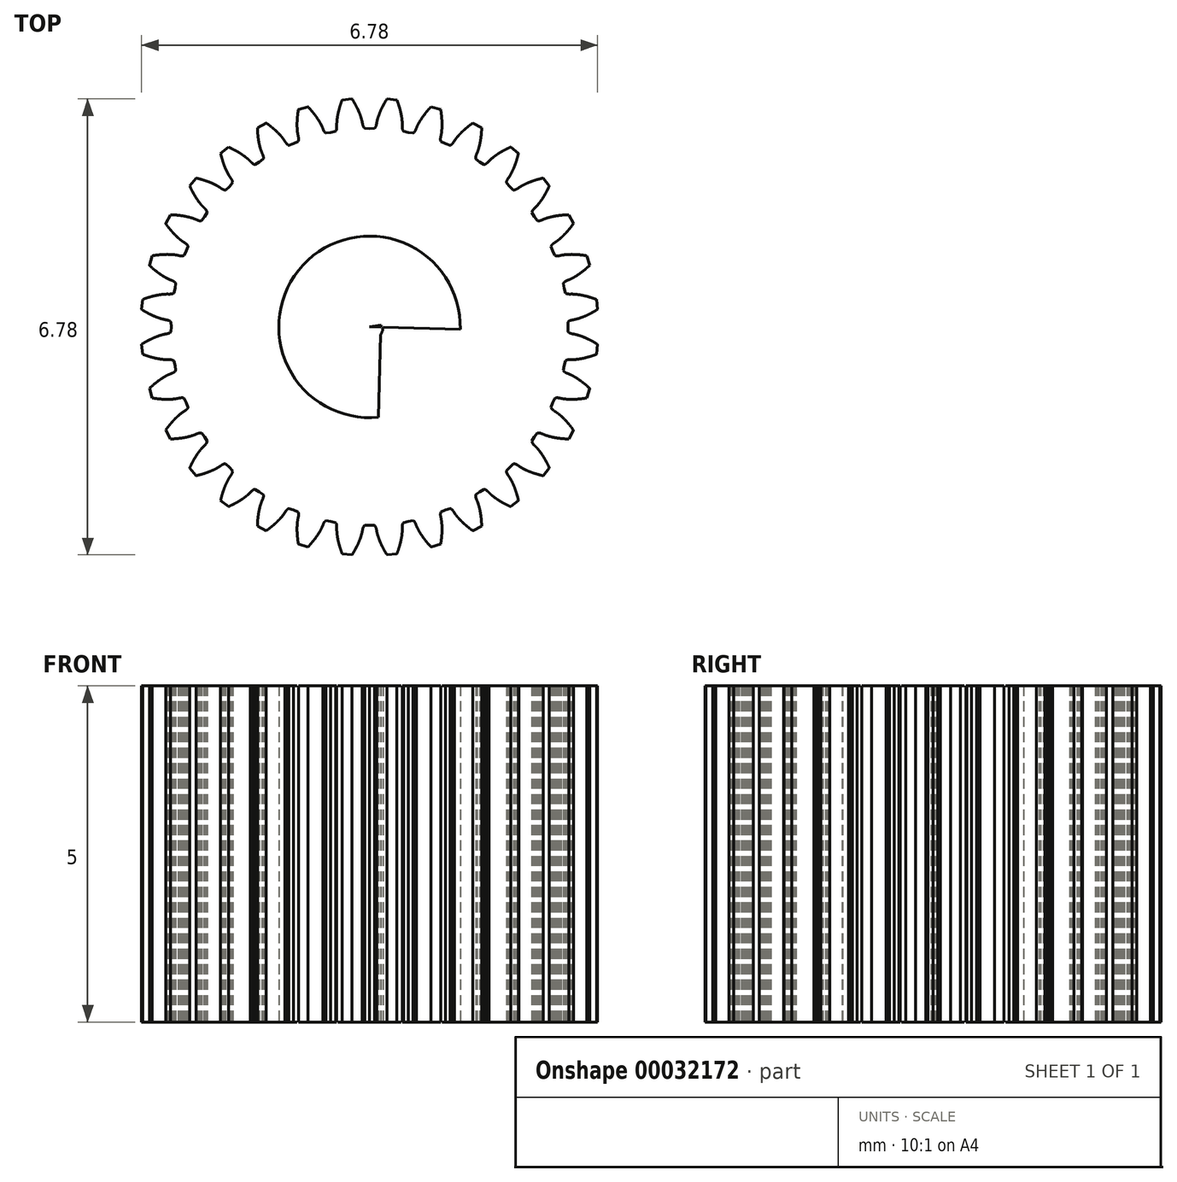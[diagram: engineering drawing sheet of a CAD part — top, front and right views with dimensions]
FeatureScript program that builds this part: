
annotation { "Feature Type Name" : "Feature", "Feature Type Description" : "" }
export const myFeature = defineFeature(function(context is Context, id is Id, definition is map)
    precondition{}
    {
        {
            var Q0;
            Q0=qCreatedBy(makeId("Top.planeOp"),FACE);
            var sketch = newSketch(context, id + "F0", { "sketchPlane" : qUnion([Q0])});
            skCircle(sketch, "E0", {"center": v(0, 0) * mm, "radius": 32.06 * mm});
            skCircle(sketch, "E1", {"center": v(0, 0) * mm, "radius": 0.2 * mm});
            skCircle(sketch, "E2", {"center": v(0, 0) * mm, "radius": 10.35 * mm});
            skCircle(sketch, "E3", {"center": v(0, 6.3) * mm, "radius": 0.2 * mm});
            skCircle(sketch, "E4", {"center": v(5.46, -3.15) * mm, "radius": 0.2 * mm});
            skCircle(sketch, "E5", {"center": v(-5.46, -3.15) * mm, "radius": 0.2 * mm});
            skLineSegment(sketch, "E6", {"start": v(0.26, 9.75) * mm, "end": v(0.26, 9.74) * mm});
            skLineSegment(sketch, "E7", {"start": v(0.26, 9.74) * mm, "end": v(0.26, 9.74) * mm});
            skLineSegment(sketch, "E8", {"start": v(0.26, 9.74) * mm, "end": v(0.26, 9.73) * mm});
            skLineSegment(sketch, "E9", {"start": v(0.26, 9.73) * mm, "end": v(0.25, 9.73) * mm});
            skLineSegment(sketch, "E10", {"start": v(0.25, 9.73) * mm, "end": v(0.25, 9.72) * mm});
            skLineSegment(sketch, "E11", {"start": v(0.25, 9.72) * mm, "end": v(0.25, 9.72) * mm});
            skLineSegment(sketch, "E12", {"start": v(0.25, 9.72) * mm, "end": v(0.25, 9.71) * mm});
            skLineSegment(sketch, "E13", {"start": v(0.25, 9.71) * mm, "end": v(0.24, 9.7) * mm});
            skLineSegment(sketch, "E14", {"start": v(0.24, 9.7) * mm, "end": v(0.24, 9.7) * mm});
            skLineSegment(sketch, "E15", {"start": v(0.24, 9.7) * mm, "end": v(0.24, 9.69) * mm});
            skLineSegment(sketch, "E16", {"start": v(0.24, 9.69) * mm, "end": v(0.23, 9.68) * mm});
            skLineSegment(sketch, "E17", {"start": v(0.23, 9.68) * mm, "end": v(0.23, 9.68) * mm});
            skLineSegment(sketch, "E18", {"start": v(0.23, 9.68) * mm, "end": v(0.23, 9.67) * mm});
            skLineSegment(sketch, "E19", {"start": v(0.23, 9.67) * mm, "end": v(0.23, 9.67) * mm});
            skLineSegment(sketch, "E20", {"start": v(0.23, 9.67) * mm, "end": v(0.22, 9.66) * mm});
            skLineSegment(sketch, "E21", {"start": v(0.22, 9.66) * mm, "end": v(0.22, 9.66) * mm});
            skLineSegment(sketch, "E22", {"start": v(0.22, 9.66) * mm, "end": v(0.22, 9.65) * mm});
            skLineSegment(sketch, "E23", {"start": v(0.22, 9.65) * mm, "end": v(0.22, 9.65) * mm});
            skLineSegment(sketch, "E24", {"start": v(0.22, 9.65) * mm, "end": v(0.22, 9.64) * mm});
            skLineSegment(sketch, "E25", {"start": v(0.22, 9.64) * mm, "end": v(0.21, 9.64) * mm});
            skLineSegment(sketch, "E26", {"start": v(0.21, 9.64) * mm, "end": v(0.21, 9.64) * mm});
            skLineSegment(sketch, "E27", {"start": v(0.21, 9.64) * mm, "end": v(0.21, 9.63) * mm});
            skLineSegment(sketch, "E28", {"start": v(0.21, 9.63) * mm, "end": v(0.2, 9.63) * mm});
            skLineSegment(sketch, "E29", {"start": v(0.2, 9.63) * mm, "end": v(0.2, 9.62) * mm});
            skLineSegment(sketch, "E30", {"start": v(0.2, 9.62) * mm, "end": v(0.2, 9.62) * mm});
            skLineSegment(sketch, "E31", {"start": v(0.2, 9.62) * mm, "end": v(0.2, 9.61) * mm});
            skLineSegment(sketch, "E32", {"start": v(0.2, 9.61) * mm, "end": v(0.2, 9.6) * mm});
            skLineSegment(sketch, "E33", {"start": v(0.2, 9.6) * mm, "end": v(0.2, 9.6) * mm});
            skLineSegment(sketch, "E34", {"start": v(0.2, 9.6) * mm, "end": v(0.2, 9.59) * mm});
            skLineSegment(sketch, "E35", {"start": v(0.2, 9.59) * mm, "end": v(0.2, 9.58) * mm});
            skLineSegment(sketch, "E36", {"start": v(0.2, 9.58) * mm, "end": v(0.19, 9.58) * mm});
            skLineSegment(sketch, "E37", {"start": v(0.19, 9.58) * mm, "end": v(0.19, 9.57) * mm});
            skLineSegment(sketch, "E38", {"start": v(0.19, 9.57) * mm, "end": v(0.18, 9.57) * mm});
            skLineSegment(sketch, "E39", {"start": v(0.18, 9.57) * mm, "end": v(0.18, 9.56) * mm});
            skLineSegment(sketch, "E40", {"start": v(0.18, 9.56) * mm, "end": v(0.18, 9.56) * mm});
            skLineSegment(sketch, "E41", {"start": v(0.18, 9.56) * mm, "end": v(0.18, 9.55) * mm});
            skLineSegment(sketch, "E42", {"start": v(0.18, 9.55) * mm, "end": v(0.18, 9.55) * mm});
            skLineSegment(sketch, "E43", {"start": v(0.18, 9.55) * mm, "end": v(0.17, 9.54) * mm});
            skLineSegment(sketch, "E44", {"start": v(0.17, 9.54) * mm, "end": v(0.17, 9.54) * mm});
            skLineSegment(sketch, "E45", {"start": v(0.17, 9.54) * mm, "end": v(0.17, 9.53) * mm});
            skLineSegment(sketch, "E46", {"start": v(0.17, 9.53) * mm, "end": v(0.17, 9.53) * mm});
            skLineSegment(sketch, "E47", {"start": v(0.17, 9.53) * mm, "end": v(0.17, 9.52) * mm});
            skLineSegment(sketch, "E48", {"start": v(0.17, 9.52) * mm, "end": v(0.16, 9.52) * mm});
            skLineSegment(sketch, "E49", {"start": v(0.16, 9.52) * mm, "end": v(0.16, 9.51) * mm});
            skLineSegment(sketch, "E50", {"start": v(0.16, 9.51) * mm, "end": v(0.16, 9.51) * mm});
            skLineSegment(sketch, "E51", {"start": v(0.16, 9.51) * mm, "end": v(0.16, 9.5) * mm});
            skLineSegment(sketch, "E52", {"start": v(0.16, 9.5) * mm, "end": v(0.16, 9.5) * mm});
            skLineSegment(sketch, "E53", {"start": v(0.16, 9.5) * mm, "end": v(0.15, 9.5) * mm});
            skLineSegment(sketch, "E54", {"start": v(0.15, 9.5) * mm, "end": v(0.15, 9.49) * mm});
            skLineSegment(sketch, "E55", {"start": v(0.15, 9.49) * mm, "end": v(0.15, 9.48) * mm});
            skLineSegment(sketch, "E56", {"start": v(0.15, 9.48) * mm, "end": v(0.15, 9.48) * mm});
            skLineSegment(sketch, "E57", {"start": v(0.15, 9.48) * mm, "end": v(0.15, 9.47) * mm});
            skLineSegment(sketch, "E58", {"start": v(0.15, 9.47) * mm, "end": v(0.15, 9.47) * mm});
            skLineSegment(sketch, "E59", {"start": v(0.15, 9.47) * mm, "end": v(0.14, 9.47) * mm});
            skLineSegment(sketch, "E60", {"start": v(0.14, 9.47) * mm, "end": v(0.14, 9.46) * mm});
            skLineSegment(sketch, "E61", {"start": v(0.14, 9.46) * mm, "end": v(0.14, 9.46) * mm});
            skLineSegment(sketch, "E62", {"start": v(0.14, 9.46) * mm, "end": v(0.14, 9.45) * mm});
            skLineSegment(sketch, "E63", {"start": v(0.14, 9.45) * mm, "end": v(0.14, 9.45) * mm});
            skLineSegment(sketch, "E64", {"start": v(0.14, 9.45) * mm, "end": v(0.14, 9.44) * mm});
            skLineSegment(sketch, "E65", {"start": v(0.14, 9.44) * mm, "end": v(0.13, 9.44) * mm});
            skLineSegment(sketch, "E66", {"start": v(0.13, 9.44) * mm, "end": v(0.13, 9.43) * mm});
            skLineSegment(sketch, "E67", {"start": v(0.13, 9.43) * mm, "end": v(0.13, 9.43) * mm});
            skLineSegment(sketch, "E68", {"start": v(0.13, 9.43) * mm, "end": v(0.13, 9.42) * mm});
            skLineSegment(sketch, "E69", {"start": v(0.13, 9.42) * mm, "end": v(0.13, 9.42) * mm});
            skLineSegment(sketch, "E70", {"start": v(0.13, 9.42) * mm, "end": v(0.12, 9.41) * mm});
            skLineSegment(sketch, "E71", {"start": v(0.12, 9.41) * mm, "end": v(0.12, 9.4) * mm});
            skLineSegment(sketch, "E72", {"start": v(0.12, 9.4) * mm, "end": v(0.12, 9.4) * mm});
            skLineSegment(sketch, "E73", {"start": v(0.12, 9.4) * mm, "end": v(0.12, 9.39) * mm});
            skLineSegment(sketch, "E74", {"start": v(0.12, 9.39) * mm, "end": v(0.12, 9.38) * mm});
            skLineSegment(sketch, "E75", {"start": v(0.12, 9.38) * mm, "end": v(0.11, 9.38) * mm});
            skLineSegment(sketch, "E76", {"start": v(0.11, 9.38) * mm, "end": v(0.11, 9.38) * mm});
            skLineSegment(sketch, "E77", {"start": v(0.11, 9.38) * mm, "end": v(0.11, 9.37) * mm});
            skLineSegment(sketch, "E78", {"start": v(0.11, 9.37) * mm, "end": v(0.1, 9.37) * mm});
            skLineSegment(sketch, "E79", {"start": v(0.1, 9.37) * mm, "end": v(0.1, 9.36) * mm});
            skLineSegment(sketch, "E80", {"start": v(0.1, 9.36) * mm, "end": v(0.1, 9.36) * mm});
            skLineSegment(sketch, "E81", {"start": v(0.1, 9.36) * mm, "end": v(0.1, 9.35) * mm});
            skLineSegment(sketch, "E82", {"start": v(0.1, 9.35) * mm, "end": v(0.1, 9.35) * mm});
            skLineSegment(sketch, "E83", {"start": v(0.1, 9.35) * mm, "end": v(0.1, 9.34) * mm});
            skLineSegment(sketch, "E84", {"start": v(0.1, 9.34) * mm, "end": v(0.1, 9.34) * mm});
            skLineSegment(sketch, "E85", {"start": v(0.1, 9.34) * mm, "end": v(0.1, 9.33) * mm});
            skLineSegment(sketch, "E86", {"start": v(0.1, 9.33) * mm, "end": v(0.1, 9.33) * mm});
            skLineSegment(sketch, "E87", {"start": v(0.1, 9.33) * mm, "end": v(0.1, 9.32) * mm});
            skLineSegment(sketch, "E88", {"start": v(0.1, 9.32) * mm, "end": v(0.1, 9.32) * mm});
            skLineSegment(sketch, "E89", {"start": v(0.1, 9.32) * mm, "end": v(0.09, 9.31) * mm});
            skLineSegment(sketch, "E90", {"start": v(0.09, 9.31) * mm, "end": v(0.09, 9.3) * mm});
            skLineSegment(sketch, "E91", {"start": v(0.09, 9.3) * mm, "end": v(0.09, 9.3) * mm});
            skLineSegment(sketch, "E92", {"start": v(0.09, 9.3) * mm, "end": v(0, 9.3) * mm});
            skLineSegment(sketch, "E93", {"start": v(0, 9.3) * mm, "end": v(-0.09, 9.3) * mm});
            skLineSegment(sketch, "E94", {"start": v(-0.09, 9.3) * mm, "end": v(-0.09, 9.3) * mm});
            skLineSegment(sketch, "E95", {"start": v(-0.09, 9.3) * mm, "end": v(-0.09, 9.31) * mm});
            skLineSegment(sketch, "E96", {"start": v(-0.09, 9.31) * mm, "end": v(-0.1, 9.32) * mm});
            skLineSegment(sketch, "E97", {"start": v(-0.1, 9.32) * mm, "end": v(-0.1, 9.32) * mm});
            skLineSegment(sketch, "E98", {"start": v(-0.1, 9.32) * mm, "end": v(-0.1, 9.33) * mm});
            skLineSegment(sketch, "E99", {"start": v(-0.1, 9.33) * mm, "end": v(-0.1, 9.33) * mm});
            skLineSegment(sketch, "E100", {"start": v(-0.1, 9.33) * mm, "end": v(-0.1, 9.34) * mm});
            skLineSegment(sketch, "E101", {"start": v(-0.1, 9.34) * mm, "end": v(-0.1, 9.34) * mm});
            skLineSegment(sketch, "E102", {"start": v(-0.1, 9.34) * mm, "end": v(-0.1, 9.35) * mm});
            skLineSegment(sketch, "E103", {"start": v(-0.1, 9.35) * mm, "end": v(-0.1, 9.35) * mm});
            skLineSegment(sketch, "E104", {"start": v(-0.1, 9.35) * mm, "end": v(-0.1, 9.36) * mm});
            skLineSegment(sketch, "E105", {"start": v(-0.1, 9.36) * mm, "end": v(-0.1, 9.36) * mm});
            skLineSegment(sketch, "E106", {"start": v(-0.1, 9.36) * mm, "end": v(-0.1, 9.37) * mm});
            skLineSegment(sketch, "E107", {"start": v(-0.1, 9.37) * mm, "end": v(-0.11, 9.37) * mm});
            skLineSegment(sketch, "E108", {"start": v(-0.11, 9.37) * mm, "end": v(-0.11, 9.38) * mm});
            skLineSegment(sketch, "E109", {"start": v(-0.11, 9.38) * mm, "end": v(-0.11, 9.38) * mm});
            skLineSegment(sketch, "E110", {"start": v(-0.11, 9.38) * mm, "end": v(-0.12, 9.38) * mm});
            skLineSegment(sketch, "E111", {"start": v(-0.12, 9.38) * mm, "end": v(-0.12, 9.39) * mm});
            skLineSegment(sketch, "E112", {"start": v(-0.12, 9.39) * mm, "end": v(-0.12, 9.4) * mm});
            skLineSegment(sketch, "E113", {"start": v(-0.12, 9.4) * mm, "end": v(-0.12, 9.4) * mm});
            skLineSegment(sketch, "E114", {"start": v(-0.12, 9.4) * mm, "end": v(-0.12, 9.41) * mm});
            skLineSegment(sketch, "E115", {"start": v(-0.12, 9.41) * mm, "end": v(-0.13, 9.42) * mm});
            skLineSegment(sketch, "E116", {"start": v(-0.13, 9.42) * mm, "end": v(-0.13, 9.42) * mm});
            skLineSegment(sketch, "E117", {"start": v(-0.13, 9.42) * mm, "end": v(-0.13, 9.43) * mm});
            skLineSegment(sketch, "E118", {"start": v(-0.13, 9.43) * mm, "end": v(-0.13, 9.43) * mm});
            skLineSegment(sketch, "E119", {"start": v(-0.13, 9.43) * mm, "end": v(-0.13, 9.44) * mm});
            skLineSegment(sketch, "E120", {"start": v(-0.13, 9.44) * mm, "end": v(-0.14, 9.44) * mm});
            skLineSegment(sketch, "E121", {"start": v(-0.14, 9.44) * mm, "end": v(-0.14, 9.45) * mm});
            skLineSegment(sketch, "E122", {"start": v(-0.14, 9.45) * mm, "end": v(-0.14, 9.45) * mm});
            skLineSegment(sketch, "E123", {"start": v(-0.14, 9.45) * mm, "end": v(-0.14, 9.46) * mm});
            skLineSegment(sketch, "E124", {"start": v(-0.14, 9.46) * mm, "end": v(-0.14, 9.46) * mm});
            skLineSegment(sketch, "E125", {"start": v(-0.14, 9.46) * mm, "end": v(-0.14, 9.47) * mm});
            skLineSegment(sketch, "E126", {"start": v(-0.14, 9.47) * mm, "end": v(-0.15, 9.47) * mm});
            skLineSegment(sketch, "E127", {"start": v(-0.15, 9.47) * mm, "end": v(-0.15, 9.47) * mm});
            skLineSegment(sketch, "E128", {"start": v(-0.15, 9.47) * mm, "end": v(-0.15, 9.48) * mm});
            skLineSegment(sketch, "E129", {"start": v(-0.15, 9.48) * mm, "end": v(-0.15, 9.48) * mm});
            skLineSegment(sketch, "E130", {"start": v(-0.15, 9.48) * mm, "end": v(-0.15, 9.49) * mm});
            skLineSegment(sketch, "E131", {"start": v(-0.15, 9.49) * mm, "end": v(-0.15, 9.5) * mm});
            skLineSegment(sketch, "E132", {"start": v(-0.15, 9.5) * mm, "end": v(-0.16, 9.5) * mm});
            skLineSegment(sketch, "E133", {"start": v(-0.16, 9.5) * mm, "end": v(-0.16, 9.5) * mm});
            skLineSegment(sketch, "E134", {"start": v(-0.16, 9.5) * mm, "end": v(-0.16, 9.51) * mm});
            skLineSegment(sketch, "E135", {"start": v(-0.16, 9.51) * mm, "end": v(-0.16, 9.51) * mm});
            skLineSegment(sketch, "E136", {"start": v(-0.16, 9.51) * mm, "end": v(-0.16, 9.52) * mm});
            skLineSegment(sketch, "E137", {"start": v(-0.16, 9.52) * mm, "end": v(-0.17, 9.52) * mm});
            skLineSegment(sketch, "E138", {"start": v(-0.17, 9.52) * mm, "end": v(-0.17, 9.53) * mm});
            skLineSegment(sketch, "E139", {"start": v(-0.17, 9.53) * mm, "end": v(-0.17, 9.53) * mm});
            skLineSegment(sketch, "E140", {"start": v(-0.17, 9.53) * mm, "end": v(-0.17, 9.54) * mm});
            skLineSegment(sketch, "E141", {"start": v(-0.17, 9.54) * mm, "end": v(-0.17, 9.54) * mm});
            skLineSegment(sketch, "E142", {"start": v(-0.17, 9.54) * mm, "end": v(-0.18, 9.55) * mm});
            skLineSegment(sketch, "E143", {"start": v(-0.18, 9.55) * mm, "end": v(-0.18, 9.55) * mm});
            skLineSegment(sketch, "E144", {"start": v(-0.18, 9.55) * mm, "end": v(-0.18, 9.56) * mm});
            skLineSegment(sketch, "E145", {"start": v(-0.18, 9.56) * mm, "end": v(-0.18, 9.56) * mm});
            skLineSegment(sketch, "E146", {"start": v(-0.18, 9.56) * mm, "end": v(-0.18, 9.57) * mm});
            skLineSegment(sketch, "E147", {"start": v(-0.18, 9.57) * mm, "end": v(-0.19, 9.57) * mm});
            skLineSegment(sketch, "E148", {"start": v(-0.19, 9.57) * mm, "end": v(-0.19, 9.58) * mm});
            skLineSegment(sketch, "E149", {"start": v(-0.19, 9.58) * mm, "end": v(-0.2, 9.58) * mm});
            skLineSegment(sketch, "E150", {"start": v(-0.2, 9.58) * mm, "end": v(-0.2, 9.59) * mm});
            skLineSegment(sketch, "E151", {"start": v(-0.2, 9.59) * mm, "end": v(-0.2, 9.6) * mm});
            skLineSegment(sketch, "E152", {"start": v(-0.2, 9.6) * mm, "end": v(-0.2, 9.6) * mm});
            skLineSegment(sketch, "E153", {"start": v(-0.2, 9.6) * mm, "end": v(-0.2, 9.61) * mm});
            skLineSegment(sketch, "E154", {"start": v(-0.2, 9.61) * mm, "end": v(-0.2, 9.62) * mm});
            skLineSegment(sketch, "E155", {"start": v(-0.2, 9.62) * mm, "end": v(-0.2, 9.62) * mm});
            skLineSegment(sketch, "E156", {"start": v(-0.2, 9.62) * mm, "end": v(-0.2, 9.63) * mm});
            skLineSegment(sketch, "E157", {"start": v(-0.2, 9.63) * mm, "end": v(-0.21, 9.63) * mm});
            skLineSegment(sketch, "E158", {"start": v(-0.21, 9.63) * mm, "end": v(-0.21, 9.64) * mm});
            skLineSegment(sketch, "E159", {"start": v(-0.21, 9.64) * mm, "end": v(-0.21, 9.64) * mm});
            skLineSegment(sketch, "E160", {"start": v(-0.21, 9.64) * mm, "end": v(-0.22, 9.64) * mm});
            skLineSegment(sketch, "E161", {"start": v(-0.22, 9.64) * mm, "end": v(-0.22, 9.65) * mm});
            skLineSegment(sketch, "E162", {"start": v(-0.22, 9.65) * mm, "end": v(-0.22, 9.65) * mm});
            skLineSegment(sketch, "E163", {"start": v(-0.22, 9.65) * mm, "end": v(-0.22, 9.66) * mm});
            skLineSegment(sketch, "E164", {"start": v(-0.22, 9.66) * mm, "end": v(-0.22, 9.66) * mm});
            skLineSegment(sketch, "E165", {"start": v(-0.22, 9.66) * mm, "end": v(-0.23, 9.67) * mm});
            skLineSegment(sketch, "E166", {"start": v(-0.23, 9.67) * mm, "end": v(-0.23, 9.67) * mm});
            skLineSegment(sketch, "E167", {"start": v(-0.23, 9.67) * mm, "end": v(-0.23, 9.68) * mm});
            skLineSegment(sketch, "E168", {"start": v(-0.23, 9.68) * mm, "end": v(-0.23, 9.68) * mm});
            skLineSegment(sketch, "E169", {"start": v(-0.23, 9.68) * mm, "end": v(-0.24, 9.69) * mm});
            skLineSegment(sketch, "E170", {"start": v(-0.24, 9.69) * mm, "end": v(-0.24, 9.7) * mm});
            skLineSegment(sketch, "E171", {"start": v(-0.24, 9.7) * mm, "end": v(-0.24, 9.7) * mm});
            skLineSegment(sketch, "E172", {"start": v(-0.24, 9.7) * mm, "end": v(-0.25, 9.71) * mm});
            skLineSegment(sketch, "E173", {"start": v(-0.25, 9.71) * mm, "end": v(-0.25, 9.72) * mm});
            skLineSegment(sketch, "E174", {"start": v(-0.25, 9.72) * mm, "end": v(-0.25, 9.72) * mm});
            skLineSegment(sketch, "E175", {"start": v(-0.25, 9.72) * mm, "end": v(-0.25, 9.73) * mm});
            skLineSegment(sketch, "E176", {"start": v(-0.25, 9.73) * mm, "end": v(-0.26, 9.73) * mm});
            skLineSegment(sketch, "E177", {"start": v(-0.26, 9.73) * mm, "end": v(-0.26, 9.74) * mm});
            skLineSegment(sketch, "E178", {"start": v(-0.26, 9.74) * mm, "end": v(-0.26, 9.74) * mm});
            skLineSegment(sketch, "E179", {"start": v(-0.26, 9.74) * mm, "end": v(-0.26, 9.75) * mm});
            skLineSegment(sketch, "E180", {"start": v(-0.26, 9.75) * mm, "end": v(-0.38, 9.74) * mm});
            skLineSegment(sketch, "E181", {"start": v(-0.38, 9.74) * mm, "end": v(-0.38, 9.74) * mm});
            skLineSegment(sketch, "E182", {"start": v(-0.38, 9.74) * mm, "end": v(-0.39, 9.73) * mm});
            skLineSegment(sketch, "E183", {"start": v(-0.39, 9.73) * mm, "end": v(-0.39, 9.73) * mm});
            skLineSegment(sketch, "E184", {"start": v(-0.39, 9.73) * mm, "end": v(-0.39, 9.72) * mm});
            skLineSegment(sketch, "E185", {"start": v(-0.39, 9.72) * mm, "end": v(-0.4, 9.72) * mm});
            skLineSegment(sketch, "E186", {"start": v(-0.4, 9.72) * mm, "end": v(-0.4, 9.72) * mm});
            skLineSegment(sketch, "E187", {"start": v(-0.4, 9.72) * mm, "end": v(-0.4, 9.71) * mm});
            skLineSegment(sketch, "E188", {"start": v(-0.4, 9.71) * mm, "end": v(-0.4, 9.7) * mm});
            skLineSegment(sketch, "E189", {"start": v(-0.4, 9.7) * mm, "end": v(-0.4, 9.7) * mm});
            skLineSegment(sketch, "E190", {"start": v(-0.4, 9.7) * mm, "end": v(-0.4, 9.69) * mm});
            skLineSegment(sketch, "E191", {"start": v(-0.4, 9.69) * mm, "end": v(-0.4, 9.68) * mm});
            skLineSegment(sketch, "E192", {"start": v(-0.4, 9.68) * mm, "end": v(-0.4, 9.68) * mm});
            skLineSegment(sketch, "E193", {"start": v(-0.4, 9.68) * mm, "end": v(-0.4, 9.67) * mm});
            skLineSegment(sketch, "E194", {"start": v(-0.4, 9.67) * mm, "end": v(-0.4, 9.67) * mm});
            skLineSegment(sketch, "E195", {"start": v(-0.4, 9.67) * mm, "end": v(-0.41, 9.66) * mm});
            skLineSegment(sketch, "E196", {"start": v(-0.41, 9.66) * mm, "end": v(-0.41, 9.66) * mm});
            skLineSegment(sketch, "E197", {"start": v(-0.41, 9.66) * mm, "end": v(-0.42, 9.65) * mm});
            skLineSegment(sketch, "E198", {"start": v(-0.42, 9.65) * mm, "end": v(-0.42, 9.65) * mm});
            skLineSegment(sketch, "E199", {"start": v(-0.42, 9.65) * mm, "end": v(-0.42, 9.64) * mm});
            skLineSegment(sketch, "E200", {"start": v(-0.42, 9.64) * mm, "end": v(-0.42, 9.64) * mm});
            skLineSegment(sketch, "E201", {"start": v(-0.42, 9.64) * mm, "end": v(-0.42, 9.63) * mm});
            skLineSegment(sketch, "E202", {"start": v(-0.42, 9.63) * mm, "end": v(-0.42, 9.63) * mm});
            skLineSegment(sketch, "E203", {"start": v(-0.42, 9.63) * mm, "end": v(-0.43, 9.62) * mm});
            skLineSegment(sketch, "E204", {"start": v(-0.43, 9.62) * mm, "end": v(-0.43, 9.62) * mm});
            skLineSegment(sketch, "E205", {"start": v(-0.43, 9.62) * mm, "end": v(-0.43, 9.61) * mm});
            skLineSegment(sketch, "E206", {"start": v(-0.43, 9.61) * mm, "end": v(-0.43, 9.6) * mm});
            skLineSegment(sketch, "E207", {"start": v(-0.43, 9.6) * mm, "end": v(-0.43, 9.6) * mm});
            skLineSegment(sketch, "E208", {"start": v(-0.43, 9.6) * mm, "end": v(-0.44, 9.6) * mm});
            skLineSegment(sketch, "E209", {"start": v(-0.44, 9.6) * mm, "end": v(-0.44, 9.6) * mm});
            skLineSegment(sketch, "E210", {"start": v(-0.44, 9.6) * mm, "end": v(-0.44, 9.59) * mm});
            skLineSegment(sketch, "E211", {"start": v(-0.44, 9.59) * mm, "end": v(-0.44, 9.58) * mm});
            skLineSegment(sketch, "E212", {"start": v(-0.44, 9.58) * mm, "end": v(-0.44, 9.58) * mm});
            skLineSegment(sketch, "E213", {"start": v(-0.44, 9.58) * mm, "end": v(-0.44, 9.57) * mm});
            skLineSegment(sketch, "E214", {"start": v(2.96, -0.58) * mm, "end": v(2.96, -0.58) * mm});
            skLineSegment(sketch, "E215", {"start": v(2.96, -0.58) * mm, "end": v(2.95, -0.58) * mm});
            skLineSegment(sketch, "E216", {"start": v(2.95, -0.58) * mm, "end": v(2.95, -0.58) * mm});
            skLineSegment(sketch, "E217", {"start": v(2.95, -0.58) * mm, "end": v(2.94, -0.57) * mm});
            skLineSegment(sketch, "E218", {"start": v(2.94, -0.57) * mm, "end": v(2.94, -0.57) * mm});
            skLineSegment(sketch, "E219", {"start": v(2.94, -0.57) * mm, "end": v(2.93, -0.57) * mm});
            skLineSegment(sketch, "E220", {"start": v(2.93, -0.57) * mm, "end": v(2.93, -0.57) * mm});
            skLineSegment(sketch, "E221", {"start": v(2.93, -0.57) * mm, "end": v(2.92, -0.56) * mm});
            skLineSegment(sketch, "E222", {"start": v(2.92, -0.56) * mm, "end": v(2.92, -0.56) * mm});
            skLineSegment(sketch, "E223", {"start": v(2.92, -0.56) * mm, "end": v(2.91, -0.56) * mm});
            skLineSegment(sketch, "E224", {"start": v(2.91, -0.56) * mm, "end": v(2.9, -0.56) * mm});
            skLineSegment(sketch, "E225", {"start": v(2.9, -0.56) * mm, "end": v(2.9, -0.56) * mm});
            skLineSegment(sketch, "E226", {"start": v(2.9, -0.56) * mm, "end": v(2.9, -0.55) * mm});
            skLineSegment(sketch, "E227", {"start": v(2.9, -0.55) * mm, "end": v(2.9, -0.55) * mm});
            skLineSegment(sketch, "E228", {"start": v(2.9, -0.55) * mm, "end": v(2.89, -0.55) * mm});
            skLineSegment(sketch, "E229", {"start": v(2.89, -0.55) * mm, "end": v(2.88, -0.55) * mm});
            skLineSegment(sketch, "E230", {"start": v(2.88, -0.55) * mm, "end": v(2.88, -0.55) * mm});
            skLineSegment(sketch, "E231", {"start": v(2.88, -0.55) * mm, "end": v(2.87, -0.55) * mm});
            skLineSegment(sketch, "E232", {"start": v(2.87, -0.55) * mm, "end": v(2.87, -0.55) * mm});
            skLineSegment(sketch, "E233", {"start": v(2.87, -0.55) * mm, "end": v(2.87, -0.54) * mm});
            skLineSegment(sketch, "E234", {"start": v(2.87, -0.54) * mm, "end": v(2.86, -0.54) * mm});
            skLineSegment(sketch, "E235", {"start": v(2.86, -0.54) * mm, "end": v(2.86, -0.54) * mm});
            skLineSegment(sketch, "E236", {"start": v(2.86, -0.54) * mm, "end": v(2.85, -0.54) * mm});
            skLineSegment(sketch, "E237", {"start": v(2.85, -0.54) * mm, "end": v(2.85, -0.54) * mm});
            skLineSegment(sketch, "E238", {"start": v(2.85, -0.54) * mm, "end": v(2.85, -0.53) * mm});
            skLineSegment(sketch, "E239", {"start": v(2.85, -0.53) * mm, "end": v(2.84, -0.53) * mm});
            skLineSegment(sketch, "E240", {"start": v(2.84, -0.53) * mm, "end": v(2.84, -0.53) * mm});
            skLineSegment(sketch, "E241", {"start": v(2.84, -0.53) * mm, "end": v(2.83, -0.53) * mm});
            skLineSegment(sketch, "E242", {"start": v(2.83, -0.53) * mm, "end": v(2.83, -0.53) * mm});
            skLineSegment(sketch, "E243", {"start": v(2.83, -0.53) * mm, "end": v(2.82, -0.52) * mm});
            skLineSegment(sketch, "E244", {"start": v(2.82, -0.52) * mm, "end": v(2.82, -0.52) * mm});
            skLineSegment(sketch, "E245", {"start": v(2.82, -0.52) * mm, "end": v(2.81, -0.51) * mm});
            skLineSegment(sketch, "E246", {"start": v(2.81, -0.51) * mm, "end": v(2.8, -0.5) * mm});
            skLineSegment(sketch, "E247", {"start": v(2.8, -0.5) * mm, "end": v(2.82, -0.43) * mm});
            skLineSegment(sketch, "E248", {"start": v(2.82, -0.43) * mm, "end": v(2.83, -0.36) * mm});
            skLineSegment(sketch, "E249", {"start": v(2.83, -0.36) * mm, "end": v(2.84, -0.35) * mm});
            skLineSegment(sketch, "E250", {"start": v(2.84, -0.35) * mm, "end": v(2.84, -0.35) * mm});
            skLineSegment(sketch, "E251", {"start": v(2.84, -0.35) * mm, "end": v(2.85, -0.35) * mm});
            skLineSegment(sketch, "E252", {"start": v(2.85, -0.35) * mm, "end": v(2.85, -0.35) * mm});
            skLineSegment(sketch, "E253", {"start": v(2.85, -0.35) * mm, "end": v(2.86, -0.35) * mm});
            skLineSegment(sketch, "E254", {"start": v(2.86, -0.35) * mm, "end": v(2.86, -0.34) * mm});
            skLineSegment(sketch, "E255", {"start": v(2.86, -0.34) * mm, "end": v(2.87, -0.34) * mm});
            skLineSegment(sketch, "E256", {"start": v(2.87, -0.34) * mm, "end": v(2.87, -0.34) * mm});
            skLineSegment(sketch, "E257", {"start": v(2.87, -0.34) * mm, "end": v(2.88, -0.34) * mm});
            skLineSegment(sketch, "E258", {"start": v(2.88, -0.34) * mm, "end": v(2.88, -0.34) * mm});
            skLineSegment(sketch, "E259", {"start": v(2.88, -0.34) * mm, "end": v(2.89, -0.34) * mm});
            skLineSegment(sketch, "E260", {"start": v(2.89, -0.34) * mm, "end": v(2.9, -0.34) * mm});
            skLineSegment(sketch, "E261", {"start": v(2.9, -0.34) * mm, "end": v(2.9, -0.34) * mm});
            skLineSegment(sketch, "E262", {"start": v(2.9, -0.34) * mm, "end": v(2.91, -0.34) * mm});
            skLineSegment(sketch, "E263", {"start": v(2.91, -0.34) * mm, "end": v(2.92, -0.34) * mm});
            skLineSegment(sketch, "E264", {"start": v(2.92, -0.34) * mm, "end": v(2.92, -0.34) * mm});
            skLineSegment(sketch, "E265", {"start": v(2.92, -0.34) * mm, "end": v(2.93, -0.34) * mm});
            skLineSegment(sketch, "E266", {"start": v(2.93, -0.34) * mm, "end": v(2.93, -0.34) * mm});
            skLineSegment(sketch, "E267", {"start": v(2.93, -0.34) * mm, "end": v(2.94, -0.34) * mm});
            skLineSegment(sketch, "E268", {"start": v(2.94, -0.34) * mm, "end": v(2.94, -0.34) * mm});
            skLineSegment(sketch, "E269", {"start": v(2.94, -0.34) * mm, "end": v(2.95, -0.34) * mm});
            skLineSegment(sketch, "E270", {"start": v(2.95, -0.34) * mm, "end": v(2.95, -0.34) * mm});
            skLineSegment(sketch, "E271", {"start": v(2.95, -0.34) * mm, "end": v(2.96, -0.34) * mm});
            skLineSegment(sketch, "E272", {"start": v(2.96, -0.34) * mm, "end": v(2.96, -0.34) * mm});
            skLineSegment(sketch, "E273", {"start": v(2.96, -0.34) * mm, "end": v(2.97, -0.34) * mm});
            skLineSegment(sketch, "E274", {"start": v(2.97, -0.34) * mm, "end": v(2.97, -0.33) * mm});
            skLineSegment(sketch, "E275", {"start": v(2.97, -0.33) * mm, "end": v(2.98, -0.33) * mm});
            skLineSegment(sketch, "E276", {"start": v(2.98, -0.33) * mm, "end": v(2.98, -0.33) * mm});
            skLineSegment(sketch, "E277", {"start": v(2.98, -0.33) * mm, "end": v(2.99, -0.33) * mm});
            skLineSegment(sketch, "E278", {"start": v(2.99, -0.33) * mm, "end": v(3, -0.33) * mm});
            skLineSegment(sketch, "E279", {"start": v(3, -0.33) * mm, "end": v(3, -0.33) * mm});
            skLineSegment(sketch, "E280", {"start": v(3, -0.33) * mm, "end": v(3.01, -0.33) * mm});
            skLineSegment(sketch, "E281", {"start": v(3.01, -0.33) * mm, "end": v(3.02, -0.33) * mm});
            skLineSegment(sketch, "E282", {"start": v(3.02, -0.33) * mm, "end": v(3.02, -0.33) * mm});
            skLineSegment(sketch, "E283", {"start": v(3.02, -0.33) * mm, "end": v(3.03, -0.33) * mm});
            skLineSegment(sketch, "E284", {"start": v(3.03, -0.33) * mm, "end": v(3.03, -0.33) * mm});
            skLineSegment(sketch, "E285", {"start": v(3.03, -0.33) * mm, "end": v(3.04, -0.32) * mm});
            skLineSegment(sketch, "E286", {"start": v(3.04, -0.32) * mm, "end": v(3.04, -0.32) * mm});
            skLineSegment(sketch, "E287", {"start": v(3.04, -0.32) * mm, "end": v(3.05, -0.32) * mm});
            skLineSegment(sketch, "E288", {"start": v(3.05, -0.32) * mm, "end": v(3.05, -0.32) * mm});
            skLineSegment(sketch, "E289", {"start": v(3.05, -0.32) * mm, "end": v(3.06, -0.32) * mm});
            skLineSegment(sketch, "E290", {"start": v(3.06, -0.32) * mm, "end": v(3.06, -0.32) * mm});
            skLineSegment(sketch, "E291", {"start": v(3.06, -0.32) * mm, "end": v(3.07, -0.32) * mm});
            skLineSegment(sketch, "E292", {"start": v(3.07, -0.32) * mm, "end": v(3.07, -0.32) * mm});
            skLineSegment(sketch, "E293", {"start": v(3.07, -0.32) * mm, "end": v(3.08, -0.32) * mm});
            skLineSegment(sketch, "E294", {"start": v(3.08, -0.32) * mm, "end": v(3.08, -0.31) * mm});
            skLineSegment(sketch, "E295", {"start": v(3.08, -0.31) * mm, "end": v(3.09, -0.31) * mm});
            skLineSegment(sketch, "E296", {"start": v(3.09, -0.31) * mm, "end": v(3.1, -0.31) * mm});
            skLineSegment(sketch, "E297", {"start": v(3.1, -0.31) * mm, "end": v(3.1, -0.31) * mm});
            skLineSegment(sketch, "E298", {"start": v(3.1, -0.31) * mm, "end": v(3.1, -0.3) * mm});
            skLineSegment(sketch, "E299", {"start": v(3.1, -0.3) * mm, "end": v(3.1, -0.3) * mm});
            skLineSegment(sketch, "E300", {"start": v(3.1, -0.3) * mm, "end": v(3.11, -0.3) * mm});
            skLineSegment(sketch, "E301", {"start": v(3.11, -0.3) * mm, "end": v(3.12, -0.3) * mm});
            skLineSegment(sketch, "E302", {"start": v(3.12, -0.3) * mm, "end": v(3.12, -0.3) * mm});
            skLineSegment(sketch, "E303", {"start": v(3.12, -0.3) * mm, "end": v(3.13, -0.3) * mm});
            skLineSegment(sketch, "E304", {"start": v(3.13, -0.3) * mm, "end": v(3.13, -0.3) * mm});
            skLineSegment(sketch, "E305", {"start": v(3.13, -0.3) * mm, "end": v(3.14, -0.3) * mm});
            skLineSegment(sketch, "E306", {"start": v(3.14, -0.3) * mm, "end": v(3.14, -0.3) * mm});
            skLineSegment(sketch, "E307", {"start": v(3.14, -0.3) * mm, "end": v(3.15, -0.3) * mm});
            skLineSegment(sketch, "E308", {"start": v(3.15, -0.3) * mm, "end": v(3.15, -0.3) * mm});
            skLineSegment(sketch, "E309", {"start": v(3.15, -0.3) * mm, "end": v(3.16, -0.3) * mm});
            skLineSegment(sketch, "E310", {"start": v(3.16, -0.3) * mm, "end": v(3.16, -0.3) * mm});
            skLineSegment(sketch, "E311", {"start": v(3.16, -0.3) * mm, "end": v(3.17, -0.29) * mm});
            skLineSegment(sketch, "E312", {"start": v(3.17, -0.29) * mm, "end": v(3.17, -0.29) * mm});
            skLineSegment(sketch, "E313", {"start": v(3.17, -0.29) * mm, "end": v(3.18, -0.29) * mm});
            skLineSegment(sketch, "E314", {"start": v(3.18, -0.29) * mm, "end": v(3.18, -0.28) * mm});
            skLineSegment(sketch, "E315", {"start": v(3.18, -0.28) * mm, "end": v(3.19, -0.28) * mm});
            skLineSegment(sketch, "E316", {"start": v(3.19, -0.28) * mm, "end": v(3.2, -0.28) * mm});
            skLineSegment(sketch, "E317", {"start": v(3.2, -0.28) * mm, "end": v(3.2, -0.28) * mm});
            skLineSegment(sketch, "E318", {"start": v(3.2, -0.28) * mm, "end": v(3.21, -0.27) * mm});
            skLineSegment(sketch, "E319", {"start": v(3.21, -0.27) * mm, "end": v(3.22, -0.27) * mm});
            skLineSegment(sketch, "E320", {"start": v(3.22, -0.27) * mm, "end": v(3.22, -0.27) * mm});
            skLineSegment(sketch, "E321", {"start": v(3.22, -0.27) * mm, "end": v(3.23, -0.27) * mm});
            skLineSegment(sketch, "E322", {"start": v(3.23, -0.27) * mm, "end": v(3.23, -0.27) * mm});
            skLineSegment(sketch, "E323", {"start": v(3.23, -0.27) * mm, "end": v(3.24, -0.26) * mm});
            skLineSegment(sketch, "E324", {"start": v(3.24, -0.26) * mm, "end": v(3.24, -0.26) * mm});
            skLineSegment(sketch, "E325", {"start": v(3.24, -0.26) * mm, "end": v(3.25, -0.26) * mm});
            skLineSegment(sketch, "E326", {"start": v(3.25, -0.26) * mm, "end": v(3.25, -0.26) * mm});
            skLineSegment(sketch, "E327", {"start": v(3.25, -0.26) * mm, "end": v(3.26, -0.26) * mm});
            skLineSegment(sketch, "E328", {"start": v(3.26, -0.26) * mm, "end": v(3.26, -0.25) * mm});
            skLineSegment(sketch, "E329", {"start": v(3.26, -0.25) * mm, "end": v(3.27, -0.25) * mm});
            skLineSegment(sketch, "E330", {"start": v(3.27, -0.25) * mm, "end": v(3.27, -0.25) * mm});
            skLineSegment(sketch, "E331", {"start": v(3.27, -0.25) * mm, "end": v(3.28, -0.25) * mm});
            skLineSegment(sketch, "E332", {"start": v(3.28, -0.25) * mm, "end": v(3.28, -0.25) * mm});
            skLineSegment(sketch, "E333", {"start": v(3.28, -0.25) * mm, "end": v(3.29, -0.24) * mm});
            skLineSegment(sketch, "E334", {"start": v(3.29, -0.24) * mm, "end": v(3.3, -0.24) * mm});
            skLineSegment(sketch, "E335", {"start": v(3.3, -0.24) * mm, "end": v(3.3, -0.1) * mm});
            skLineSegment(sketch, "E336", {"start": v(3.3, -0.1) * mm, "end": v(3.3, -0.1) * mm});
            skLineSegment(sketch, "E337", {"start": v(3.3, -0.1) * mm, "end": v(3.29, -0.09) * mm});
            skLineSegment(sketch, "E338", {"start": v(3.29, -0.09) * mm, "end": v(3.29, -0.09) * mm});
            skLineSegment(sketch, "E339", {"start": v(3.29, -0.09) * mm, "end": v(3.28, -0.08) * mm});
            skLineSegment(sketch, "E340", {"start": v(3.28, -0.08) * mm, "end": v(3.28, -0.08) * mm});
            skLineSegment(sketch, "E341", {"start": v(3.28, -0.08) * mm, "end": v(3.27, -0.08) * mm});
            skLineSegment(sketch, "E342", {"start": v(3.27, -0.08) * mm, "end": v(3.27, -0.08) * mm});
            skLineSegment(sketch, "E343", {"start": v(3.27, -0.08) * mm, "end": v(3.26, -0.07) * mm});
            skLineSegment(sketch, "E344", {"start": v(3.26, -0.07) * mm, "end": v(3.26, -0.07) * mm});
            skLineSegment(sketch, "E345", {"start": v(3.26, -0.07) * mm, "end": v(3.25, -0.07) * mm});
            skLineSegment(sketch, "E346", {"start": v(3.25, -0.07) * mm, "end": v(3.25, -0.07) * mm});
            skLineSegment(sketch, "E347", {"start": v(3.25, -0.07) * mm, "end": v(3.25, -0.06) * mm});
            skLineSegment(sketch, "E348", {"start": v(3.25, -0.06) * mm, "end": v(3.24, -0.06) * mm});
            skLineSegment(sketch, "E349", {"start": v(3.24, -0.06) * mm, "end": v(3.24, -0.06) * mm});
            skLineSegment(sketch, "E350", {"start": v(3.24, -0.06) * mm, "end": v(3.23, -0.06) * mm});
            skLineSegment(sketch, "E351", {"start": v(3.23, -0.06) * mm, "end": v(3.23, -0.06) * mm});
            skLineSegment(sketch, "E352", {"start": v(3.23, -0.06) * mm, "end": v(3.22, -0.05) * mm});
            skLineSegment(sketch, "E353", {"start": v(3.22, -0.05) * mm, "end": v(3.22, -0.05) * mm});
            skLineSegment(sketch, "E354", {"start": v(3.22, -0.05) * mm, "end": v(3.21, -0.05) * mm});
            skLineSegment(sketch, "E355", {"start": v(3.21, -0.05) * mm, "end": v(3.2, -0.05) * mm});
            skLineSegment(sketch, "E356", {"start": v(3.2, -0.05) * mm, "end": v(3.2, -0.04) * mm});
            skLineSegment(sketch, "E357", {"start": v(3.2, -0.04) * mm, "end": v(3.2, -0.04) * mm});
            skLineSegment(sketch, "E358", {"start": v(3.2, -0.04) * mm, "end": v(3.19, -0.04) * mm});
            skLineSegment(sketch, "E359", {"start": v(3.19, -0.04) * mm, "end": v(3.18, -0.03) * mm});
            skLineSegment(sketch, "E360", {"start": v(3.18, -0.03) * mm, "end": v(3.18, -0.03) * mm});
            skLineSegment(sketch, "E361", {"start": v(3.18, -0.03) * mm, "end": v(3.17, -0.03) * mm});
            skLineSegment(sketch, "E362", {"start": v(3.17, -0.03) * mm, "end": v(3.17, -0.03) * mm});
            skLineSegment(sketch, "E363", {"start": v(3.17, -0.03) * mm, "end": v(3.16, -0.03) * mm});
            skLineSegment(sketch, "E364", {"start": v(3.16, -0.03) * mm, "end": v(3.16, -0.02) * mm});
            skLineSegment(sketch, "E365", {"start": v(3.16, -0.02) * mm, "end": v(3.16, -0.02) * mm});
            skLineSegment(sketch, "E366", {"start": v(3.16, -0.02) * mm, "end": v(3.15, -0.02) * mm});
            skLineSegment(sketch, "E367", {"start": v(3.15, -0.02) * mm, "end": v(3.15, -0.02) * mm});
            skLineSegment(sketch, "E368", {"start": v(3.15, -0.02) * mm, "end": v(3.14, -0.02) * mm});
            skLineSegment(sketch, "E369", {"start": v(3.14, -0.02) * mm, "end": v(3.14, -0.01) * mm});
            skLineSegment(sketch, "E370", {"start": v(3.14, -0.01) * mm, "end": v(3.13, -0.01) * mm});
            skLineSegment(sketch, "E371", {"start": v(3.13, -0.01) * mm, "end": v(3.13, -0.01) * mm});
            skLineSegment(sketch, "E372", {"start": v(3.13, -0.01) * mm, "end": v(3.12, 0) * mm});
            skLineSegment(sketch, "E373", {"start": v(3.12, 0) * mm, "end": v(3.12, 0) * mm});
            skLineSegment(sketch, "E374", {"start": v(3.12, 0) * mm, "end": v(3.11, 0) * mm});
            skLineSegment(sketch, "E375", {"start": v(3.11, 0) * mm, "end": v(3.1, 0) * mm});
            skLineSegment(sketch, "E376", {"start": v(3.1, 0) * mm, "end": v(3.1, 0) * mm});
            skLineSegment(sketch, "E377", {"start": v(3.1, 0) * mm, "end": v(3.09, 0) * mm});
            skLineSegment(sketch, "E378", {"start": v(3.09, 0) * mm, "end": v(3.08, 0) * mm});
            skLineSegment(sketch, "E379", {"start": v(3.08, 0) * mm, "end": v(3.08, 0) * mm});
            skLineSegment(sketch, "E380", {"start": v(3.08, 0) * mm, "end": v(3.07, 0) * mm});
            skLineSegment(sketch, "E381", {"start": v(3.07, 0) * mm, "end": v(3.07, 0.01) * mm});
            skLineSegment(sketch, "E382", {"start": v(3.07, 0.01) * mm, "end": v(3.07, 0.01) * mm});
            skLineSegment(sketch, "E383", {"start": v(3.07, 0.01) * mm, "end": v(3.06, 0.01) * mm});
            skLineSegment(sketch, "E384", {"start": v(3.06, 0.01) * mm, "end": v(3.06, 0.01) * mm});
            skLineSegment(sketch, "E385", {"start": v(3.06, 0.01) * mm, "end": v(3.05, 0.02) * mm});
            skLineSegment(sketch, "E386", {"start": v(3.05, 0.02) * mm, "end": v(3.05, 0.02) * mm});
            skLineSegment(sketch, "E387", {"start": v(3.05, 0.02) * mm, "end": v(3.04, 0.02) * mm});
            skLineSegment(sketch, "E388", {"start": v(3.04, 0.02) * mm, "end": v(3.04, 0.02) * mm});
            skLineSegment(sketch, "E389", {"start": v(3.04, 0.02) * mm, "end": v(3.03, 0.02) * mm});
            skLineSegment(sketch, "E390", {"start": v(3.03, 0.02) * mm, "end": v(3.03, 0.02) * mm});
            skLineSegment(sketch, "E391", {"start": v(3.03, 0.02) * mm, "end": v(3.02, 0.03) * mm});
            skLineSegment(sketch, "E392", {"start": v(3.02, 0.03) * mm, "end": v(3.02, 0.03) * mm});
            skLineSegment(sketch, "E393", {"start": v(3.02, 0.03) * mm, "end": v(3.01, 0.03) * mm});
            skLineSegment(sketch, "E394", {"start": v(3.01, 0.03) * mm, "end": v(3, 0.03) * mm});
            skLineSegment(sketch, "E395", {"start": v(3, 0.03) * mm, "end": v(3, 0.03) * mm});
            skLineSegment(sketch, "E396", {"start": v(3, 0.03) * mm, "end": v(2.99, 0.03) * mm});
            skLineSegment(sketch, "E397", {"start": v(2.99, 0.03) * mm, "end": v(2.98, 0.03) * mm});
            skLineSegment(sketch, "E398", {"start": v(2.98, 0.03) * mm, "end": v(2.98, 0.03) * mm});
            skLineSegment(sketch, "E399", {"start": v(2.98, 0.03) * mm, "end": v(2.98, 0.04) * mm});
            skLineSegment(sketch, "E400", {"start": v(2.98, 0.04) * mm, "end": v(2.97, 0.04) * mm});
            skLineSegment(sketch, "E401", {"start": v(2.97, 0.04) * mm, "end": v(2.97, 0.04) * mm});
            skLineSegment(sketch, "E402", {"start": v(2.97, 0.04) * mm, "end": v(2.96, 0.04) * mm});
            skLineSegment(sketch, "E403", {"start": v(2.96, 0.04) * mm, "end": v(2.96, 0.04) * mm});
            skLineSegment(sketch, "E404", {"start": v(2.96, 0.04) * mm, "end": v(2.95, 0.04) * mm});
            skLineSegment(sketch, "E405", {"start": v(2.95, 0.04) * mm, "end": v(2.95, 0.04) * mm});
            skLineSegment(sketch, "E406", {"start": v(2.95, 0.04) * mm, "end": v(2.94, 0.04) * mm});
            skLineSegment(sketch, "E407", {"start": v(2.94, 0.04) * mm, "end": v(2.94, 0.04) * mm});
            skLineSegment(sketch, "E408", {"start": v(2.94, 0.04) * mm, "end": v(2.93, 0.04) * mm});
            skLineSegment(sketch, "E409", {"start": v(2.93, 0.04) * mm, "end": v(2.93, 0.04) * mm});
            skLineSegment(sketch, "E410", {"start": v(2.93, 0.04) * mm, "end": v(2.92, 0.04) * mm});
            skLineSegment(sketch, "E411", {"start": v(2.92, 0.04) * mm, "end": v(2.92, 0.04) * mm});
            skLineSegment(sketch, "E412", {"start": v(2.92, 0.04) * mm, "end": v(2.91, 0.04) * mm});
            skLineSegment(sketch, "E413", {"start": v(2.91, 0.04) * mm, "end": v(2.9, 0.05) * mm});
            skLineSegment(sketch, "E414", {"start": v(2.9, 0.05) * mm, "end": v(2.9, 0.05) * mm});
            skLineSegment(sketch, "E415", {"start": v(2.9, 0.05) * mm, "end": v(2.89, 0.05) * mm});
            skLineSegment(sketch, "E416", {"start": v(2.89, 0.05) * mm, "end": v(2.88, 0.05) * mm});
            skLineSegment(sketch, "E417", {"start": v(2.88, 0.05) * mm, "end": v(2.88, 0.05) * mm});
            skLineSegment(sketch, "E418", {"start": v(2.88, 0.05) * mm, "end": v(2.87, 0.06) * mm});
            skLineSegment(sketch, "E419", {"start": v(2.87, 0.06) * mm, "end": v(2.87, 0.06) * mm});
            skLineSegment(sketch, "E420", {"start": v(2.87, 0.06) * mm, "end": v(2.86, 0.06) * mm});
            skLineSegment(sketch, "E421", {"start": v(2.86, 0.06) * mm, "end": v(2.86, 0.07) * mm});
            skLineSegment(sketch, "E422", {"start": v(2.86, 0.07) * mm, "end": v(2.85, 0.07) * mm});
            skLineSegment(sketch, "E423", {"start": v(2.95, 6.23) * mm, "end": v(2.95, 6.3) * mm});
            skLineSegment(sketch, "E424", {"start": v(2.95, 6.3) * mm, "end": v(2.95, 6.37) * mm});
            skLineSegment(sketch, "E425", {"start": v(2.95, 6.37) * mm, "end": v(2.96, 6.38) * mm});
            skLineSegment(sketch, "E426", {"start": v(2.96, 6.38) * mm, "end": v(2.96, 6.38) * mm});
            skLineSegment(sketch, "E427", {"start": v(2.96, 6.38) * mm, "end": v(2.97, 6.39) * mm});
            skLineSegment(sketch, "E428", {"start": v(2.97, 6.39) * mm, "end": v(2.97, 6.39) * mm});
            skLineSegment(sketch, "E429", {"start": v(2.97, 6.39) * mm, "end": v(2.98, 6.4) * mm});
            skLineSegment(sketch, "E430", {"start": v(2.98, 6.4) * mm, "end": v(2.98, 6.4) * mm});
            skLineSegment(sketch, "E431", {"start": v(2.98, 6.4) * mm, "end": v(2.99, 6.4) * mm});
            skLineSegment(sketch, "E432", {"start": v(2.99, 6.4) * mm, "end": v(3, 6.4) * mm});
            skLineSegment(sketch, "E433", {"start": v(3, 6.4) * mm, "end": v(3, 6.4) * mm});
            skLineSegment(sketch, "E434", {"start": v(3, 6.4) * mm, "end": v(3.01, 6.4) * mm});
            skLineSegment(sketch, "E435", {"start": v(3.01, 6.4) * mm, "end": v(3.02, 6.4) * mm});
            skLineSegment(sketch, "E436", {"start": v(3.02, 6.4) * mm, "end": v(3.02, 6.4) * mm});
            skLineSegment(sketch, "E437", {"start": v(3.02, 6.4) * mm, "end": v(3.03, 6.4) * mm});
            skLineSegment(sketch, "E438", {"start": v(3.03, 6.4) * mm, "end": v(3.03, 6.4) * mm});
            skLineSegment(sketch, "E439", {"start": v(3.03, 6.4) * mm, "end": v(3.04, 6.4) * mm});
            skLineSegment(sketch, "E440", {"start": v(3.04, 6.4) * mm, "end": v(3.04, 6.4) * mm});
            skLineSegment(sketch, "E441", {"start": v(3.04, 6.4) * mm, "end": v(3.05, 6.4) * mm});
            skLineSegment(sketch, "E442", {"start": v(3.05, 6.4) * mm, "end": v(3.05, 6.4) * mm});
            skLineSegment(sketch, "E443", {"start": v(3.05, 6.4) * mm, "end": v(3.06, 6.41) * mm});
            skLineSegment(sketch, "E444", {"start": v(3.06, 6.41) * mm, "end": v(3.06, 6.41) * mm});
            skLineSegment(sketch, "E445", {"start": v(3.06, 6.41) * mm, "end": v(3.07, 6.41) * mm});
            skLineSegment(sketch, "E446", {"start": v(3.07, 6.41) * mm, "end": v(3.07, 6.42) * mm});
            skLineSegment(sketch, "E447", {"start": v(3.07, 6.42) * mm, "end": v(3.08, 6.42) * mm});
            skLineSegment(sketch, "E448", {"start": v(3.08, 6.42) * mm, "end": v(3.08, 6.42) * mm});
            skLineSegment(sketch, "E449", {"start": v(3.08, 6.42) * mm, "end": v(3.09, 6.42) * mm});
            skLineSegment(sketch, "E450", {"start": v(3.09, 6.42) * mm, "end": v(3.1, 6.42) * mm});
            skLineSegment(sketch, "E451", {"start": v(3.1, 6.42) * mm, "end": v(3.1, 6.42) * mm});
            skLineSegment(sketch, "E452", {"start": v(3.1, 6.42) * mm, "end": v(3.1, 6.43) * mm});
            skLineSegment(sketch, "E453", {"start": v(3.1, 6.43) * mm, "end": v(3.11, 6.43) * mm});
            skLineSegment(sketch, "E454", {"start": v(3.11, 6.43) * mm, "end": v(3.12, 6.43) * mm});
            skLineSegment(sketch, "E455", {"start": v(3.12, 6.43) * mm, "end": v(3.12, 6.43) * mm});
            skLineSegment(sketch, "E456", {"start": v(3.12, 6.43) * mm, "end": v(3.13, 6.43) * mm});
            skLineSegment(sketch, "E457", {"start": v(3.13, 6.43) * mm, "end": v(3.13, 6.43) * mm});
            skLineSegment(sketch, "E458", {"start": v(3.13, 6.43) * mm, "end": v(3.14, 6.43) * mm});
            skLineSegment(sketch, "E459", {"start": v(3.14, 6.43) * mm, "end": v(3.14, 6.44) * mm});
            skLineSegment(sketch, "E460", {"start": v(3.14, 6.44) * mm, "end": v(3.15, 6.44) * mm});
            skLineSegment(sketch, "E461", {"start": v(3.15, 6.44) * mm, "end": v(3.15, 6.44) * mm});
            skLineSegment(sketch, "E462", {"start": v(3.15, 6.44) * mm, "end": v(3.16, 6.44) * mm});
            skLineSegment(sketch, "E463", {"start": v(3.16, 6.44) * mm, "end": v(3.16, 6.44) * mm});
            skLineSegment(sketch, "E464", {"start": v(3.16, 6.44) * mm, "end": v(3.17, 6.45) * mm});
            skLineSegment(sketch, "E465", {"start": v(3.17, 6.45) * mm, "end": v(3.17, 6.45) * mm});
            skLineSegment(sketch, "E466", {"start": v(3.17, 6.45) * mm, "end": v(3.18, 6.45) * mm});
            skLineSegment(sketch, "E467", {"start": v(3.18, 6.45) * mm, "end": v(3.18, 6.45) * mm});
            skLineSegment(sketch, "E468", {"start": v(3.18, 6.45) * mm, "end": v(3.19, 6.45) * mm});
            skLineSegment(sketch, "E469", {"start": v(3.19, 6.45) * mm, "end": v(3.2, 6.46) * mm});
            skLineSegment(sketch, "E470", {"start": v(3.2, 6.46) * mm, "end": v(3.2, 6.46) * mm});
            skLineSegment(sketch, "E471", {"start": v(3.2, 6.46) * mm, "end": v(3.21, 6.46) * mm});
            skLineSegment(sketch, "E472", {"start": v(3.21, 6.46) * mm, "end": v(3.22, 6.47) * mm});
            skLineSegment(sketch, "E473", {"start": v(3.22, 6.47) * mm, "end": v(3.22, 6.47) * mm});
            skLineSegment(sketch, "E474", {"start": v(3.22, 6.47) * mm, "end": v(3.23, 6.47) * mm});
            skLineSegment(sketch, "E475", {"start": v(3.23, 6.47) * mm, "end": v(3.23, 6.47) * mm});
            skLineSegment(sketch, "E476", {"start": v(3.23, 6.47) * mm, "end": v(3.24, 6.48) * mm});
            skLineSegment(sketch, "E477", {"start": v(3.24, 6.48) * mm, "end": v(3.24, 6.48) * mm});
            skLineSegment(sketch, "E478", {"start": v(3.24, 6.48) * mm, "end": v(3.25, 6.48) * mm});
            skLineSegment(sketch, "E479", {"start": v(3.25, 6.48) * mm, "end": v(3.25, 6.48) * mm});
            skLineSegment(sketch, "E480", {"start": v(3.25, 6.48) * mm, "end": v(3.26, 6.48) * mm});
            skLineSegment(sketch, "E481", {"start": v(3.26, 6.48) * mm, "end": v(3.26, 6.49) * mm});
            skLineSegment(sketch, "E482", {"start": v(3.26, 6.49) * mm, "end": v(3.26, 6.49) * mm});
            skLineSegment(sketch, "E483", {"start": v(3.26, 6.49) * mm, "end": v(3.27, 6.5) * mm});
            skLineSegment(sketch, "E484", {"start": v(3.27, 6.5) * mm, "end": v(3.27, 6.5) * mm});
            skLineSegment(sketch, "E485", {"start": v(3.27, 6.5) * mm, "end": v(3.28, 6.5) * mm});
            skLineSegment(sketch, "E486", {"start": v(3.28, 6.5) * mm, "end": v(3.28, 6.5) * mm});
            skLineSegment(sketch, "E487", {"start": v(3.28, 6.5) * mm, "end": v(3.29, 6.5) * mm});
            skLineSegment(sketch, "E488", {"start": v(3.29, 6.5) * mm, "end": v(3.3, 6.5) * mm});
            skLineSegment(sketch, "E489", {"start": v(3.3, 6.5) * mm, "end": v(3.3, 6.5) * mm});
            skLineSegment(sketch, "E490", {"start": v(3.3, 6.5) * mm, "end": v(3.3, 6.51) * mm});
            skLineSegment(sketch, "E491", {"start": v(3.3, 6.51) * mm, "end": v(3.31, 6.51) * mm});
            skLineSegment(sketch, "E492", {"start": v(3.31, 6.51) * mm, "end": v(3.32, 6.52) * mm});
            skLineSegment(sketch, "E493", {"start": v(3.32, 6.52) * mm, "end": v(3.32, 6.52) * mm});
            skLineSegment(sketch, "E494", {"start": v(3.32, 6.52) * mm, "end": v(3.33, 6.52) * mm});
            skLineSegment(sketch, "E495", {"start": v(3.33, 6.52) * mm, "end": v(3.33, 6.52) * mm});
            skLineSegment(sketch, "E496", {"start": v(3.33, 6.52) * mm, "end": v(3.33, 6.53) * mm});
            skLineSegment(sketch, "E497", {"start": v(3.33, 6.53) * mm, "end": v(3.34, 6.53) * mm});
            skLineSegment(sketch, "E498", {"start": v(3.34, 6.53) * mm, "end": v(3.34, 6.53) * mm});
            skLineSegment(sketch, "E499", {"start": v(3.34, 6.53) * mm, "end": v(3.35, 6.53) * mm});
            skLineSegment(sketch, "E500", {"start": v(3.35, 6.53) * mm, "end": v(3.35, 6.54) * mm});
            skLineSegment(sketch, "E501", {"start": v(3.35, 6.54) * mm, "end": v(3.36, 6.54) * mm});
            skLineSegment(sketch, "E502", {"start": v(3.36, 6.54) * mm, "end": v(3.36, 6.54) * mm});
            skLineSegment(sketch, "E503", {"start": v(3.36, 6.54) * mm, "end": v(3.37, 6.55) * mm});
            skLineSegment(sketch, "E504", {"start": v(3.37, 6.55) * mm, "end": v(3.37, 6.55) * mm});
            skLineSegment(sketch, "E505", {"start": v(3.37, 6.55) * mm, "end": v(3.38, 6.55) * mm});
            skLineSegment(sketch, "E506", {"start": v(3.38, 6.55) * mm, "end": v(3.38, 6.55) * mm});
            skLineSegment(sketch, "E507", {"start": v(3.38, 6.55) * mm, "end": v(3.39, 6.56) * mm});
            skLineSegment(sketch, "E508", {"start": v(3.39, 6.56) * mm, "end": v(3.4, 6.56) * mm});
            skLineSegment(sketch, "E509", {"start": v(3.4, 6.56) * mm, "end": v(3.38, 6.7) * mm});
            skLineSegment(sketch, "E510", {"start": v(3.38, 6.7) * mm, "end": v(3.37, 6.7) * mm});
            skLineSegment(sketch, "E511", {"start": v(3.37, 6.7) * mm, "end": v(3.37, 6.71) * mm});
            skLineSegment(sketch, "E512", {"start": v(3.37, 6.71) * mm, "end": v(3.36, 6.71) * mm});
            skLineSegment(sketch, "E513", {"start": v(3.36, 6.71) * mm, "end": v(3.36, 6.71) * mm});
            skLineSegment(sketch, "E514", {"start": v(3.36, 6.71) * mm, "end": v(3.35, 6.72) * mm});
            skLineSegment(sketch, "E515", {"start": v(3.35, 6.72) * mm, "end": v(3.35, 6.72) * mm});
            skLineSegment(sketch, "E516", {"start": v(3.35, 6.72) * mm, "end": v(3.34, 6.72) * mm});
            skLineSegment(sketch, "E517", {"start": v(3.34, 6.72) * mm, "end": v(3.34, 6.72) * mm});
            skLineSegment(sketch, "E518", {"start": v(3.34, 6.72) * mm, "end": v(3.33, 6.72) * mm});
            skLineSegment(sketch, "E519", {"start": v(3.33, 6.72) * mm, "end": v(3.33, 6.72) * mm});
            skLineSegment(sketch, "E520", {"start": v(3.33, 6.72) * mm, "end": v(3.32, 6.73) * mm});
            skLineSegment(sketch, "E521", {"start": v(3.32, 6.73) * mm, "end": v(3.32, 6.73) * mm});
            skLineSegment(sketch, "E522", {"start": v(3.32, 6.73) * mm, "end": v(3.31, 6.73) * mm});
            skLineSegment(sketch, "E523", {"start": v(3.31, 6.73) * mm, "end": v(3.3, 6.73) * mm});
            skLineSegment(sketch, "E524", {"start": v(3.3, 6.73) * mm, "end": v(3.3, 6.73) * mm});
            skLineSegment(sketch, "E525", {"start": v(3.3, 6.73) * mm, "end": v(3.3, 6.74) * mm});
            skLineSegment(sketch, "E526", {"start": v(3.3, 6.74) * mm, "end": v(3.3, 6.74) * mm});
            skLineSegment(sketch, "E527", {"start": v(3.3, 6.74) * mm, "end": v(3.29, 6.74) * mm});
            skLineSegment(sketch, "E528", {"start": v(3.29, 6.74) * mm, "end": v(3.28, 6.74) * mm});
            skLineSegment(sketch, "E529", {"start": v(3.28, 6.74) * mm, "end": v(3.28, 6.74) * mm});
            skLineSegment(sketch, "E530", {"start": v(3.28, 6.74) * mm, "end": v(3.27, 6.74) * mm});
            skLineSegment(sketch, "E531", {"start": v(3.27, 6.74) * mm, "end": v(3.27, 6.74) * mm});
            skLineSegment(sketch, "E532", {"start": v(3.27, 6.74) * mm, "end": v(3.26, 6.75) * mm});
            skLineSegment(sketch, "E533", {"start": v(3.26, 6.75) * mm, "end": v(3.26, 6.75) * mm});
            skLineSegment(sketch, "E534", {"start": v(3.26, 6.75) * mm, "end": v(3.25, 6.75) * mm});
            skLineSegment(sketch, "E535", {"start": v(3.25, 6.75) * mm, "end": v(3.25, 6.75) * mm});
            skLineSegment(sketch, "E536", {"start": v(3.25, 6.75) * mm, "end": v(3.24, 6.75) * mm});
            skLineSegment(sketch, "E537", {"start": v(3.24, 6.75) * mm, "end": v(3.24, 6.75) * mm});
            skLineSegment(sketch, "E538", {"start": v(3.24, 6.75) * mm, "end": v(3.23, 6.75) * mm});
            skLineSegment(sketch, "E539", {"start": v(3.23, 6.75) * mm, "end": v(3.23, 6.75) * mm});
            skLineSegment(sketch, "E540", {"start": v(3.23, 6.75) * mm, "end": v(3.22, 6.76) * mm});
            skLineSegment(sketch, "E541", {"start": v(3.22, 6.76) * mm, "end": v(3.22, 6.76) * mm});
            skLineSegment(sketch, "E542", {"start": v(3.22, 6.76) * mm, "end": v(3.21, 6.76) * mm});
            skLineSegment(sketch, "E543", {"start": v(3.21, 6.76) * mm, "end": v(3.2, 6.76) * mm});
            skLineSegment(sketch, "E544", {"start": v(3.2, 6.76) * mm, "end": v(3.2, 6.76) * mm});
            skLineSegment(sketch, "E545", {"start": v(3.2, 6.76) * mm, "end": v(3.19, 6.77) * mm});
            skLineSegment(sketch, "E546", {"start": v(3.19, 6.77) * mm, "end": v(3.18, 6.77) * mm});
            skLineSegment(sketch, "E547", {"start": v(3.18, 6.77) * mm, "end": v(3.18, 6.77) * mm});
            skLineSegment(sketch, "E548", {"start": v(3.18, 6.77) * mm, "end": v(3.17, 6.77) * mm});
            skLineSegment(sketch, "E549", {"start": v(3.17, 6.77) * mm, "end": v(3.17, 6.77) * mm});
            skLineSegment(sketch, "E550", {"start": v(3.17, 6.77) * mm, "end": v(3.16, 6.77) * mm});
            skLineSegment(sketch, "E551", {"start": v(3.16, 6.77) * mm, "end": v(3.16, 6.77) * mm});
            skLineSegment(sketch, "E552", {"start": v(3.16, 6.77) * mm, "end": v(3.15, 6.77) * mm});
            skLineSegment(sketch, "E553", {"start": v(3.15, 6.77) * mm, "end": v(3.15, 6.77) * mm});
            skLineSegment(sketch, "E554", {"start": v(3.15, 6.77) * mm, "end": v(3.14, 6.77) * mm});
            skLineSegment(sketch, "E555", {"start": v(3.14, 6.77) * mm, "end": v(3.14, 6.77) * mm});
            skLineSegment(sketch, "E556", {"start": v(3.14, 6.77) * mm, "end": v(3.13, 6.78) * mm});
            skLineSegment(sketch, "E557", {"start": v(3.13, 6.78) * mm, "end": v(3.13, 6.78) * mm});
            skLineSegment(sketch, "E558", {"start": v(3.13, 6.78) * mm, "end": v(3.12, 6.78) * mm});
            skLineSegment(sketch, "E559", {"start": v(3.12, 6.78) * mm, "end": v(3.12, 6.78) * mm});
            skLineSegment(sketch, "E560", {"start": v(3.12, 6.78) * mm, "end": v(3.11, 6.78) * mm});
            skLineSegment(sketch, "E561", {"start": v(3.11, 6.78) * mm, "end": v(3.1, 6.78) * mm});
            skLineSegment(sketch, "E562", {"start": v(3.1, 6.78) * mm, "end": v(3.1, 6.78) * mm});
            skLineSegment(sketch, "E563", {"start": v(3.1, 6.78) * mm, "end": v(3.09, 6.78) * mm});
            skLineSegment(sketch, "E564", {"start": v(3.09, 6.78) * mm, "end": v(3.08, 6.78) * mm});
            skLineSegment(sketch, "E565", {"start": v(3.08, 6.78) * mm, "end": v(3.08, 6.78) * mm});
            skLineSegment(sketch, "E566", {"start": v(3.08, 6.78) * mm, "end": v(3.07, 6.78) * mm});
            skLineSegment(sketch, "E567", {"start": v(3.07, 6.78) * mm, "end": v(3.07, 6.78) * mm});
            skLineSegment(sketch, "E568", {"start": v(3.07, 6.78) * mm, "end": v(3.06, 6.78) * mm});
            skLineSegment(sketch, "E569", {"start": v(3.06, 6.78) * mm, "end": v(3.06, 6.79) * mm});
            skLineSegment(sketch, "E570", {"start": v(3.06, 6.79) * mm, "end": v(3.06, 6.79) * mm});
            skLineSegment(sketch, "E571", {"start": v(3.06, 6.79) * mm, "end": v(3.05, 6.79) * mm});
            skLineSegment(sketch, "E572", {"start": v(3.05, 6.79) * mm, "end": v(3.05, 6.79) * mm});
            skLineSegment(sketch, "E573", {"start": v(3.05, 6.79) * mm, "end": v(3.04, 6.79) * mm});
            skLineSegment(sketch, "E574", {"start": v(3.04, 6.79) * mm, "end": v(3.04, 6.79) * mm});
            skLineSegment(sketch, "E575", {"start": v(3.04, 6.79) * mm, "end": v(3.03, 6.79) * mm});
            skLineSegment(sketch, "E576", {"start": v(3.03, 6.79) * mm, "end": v(3.03, 6.79) * mm});
            skLineSegment(sketch, "E577", {"start": v(3.03, 6.79) * mm, "end": v(3.02, 6.79) * mm});
            skLineSegment(sketch, "E578", {"start": v(3.02, 6.79) * mm, "end": v(3.02, 6.79) * mm});
            skLineSegment(sketch, "E579", {"start": v(3.02, 6.79) * mm, "end": v(3.01, 6.79) * mm});
            skLineSegment(sketch, "E580", {"start": v(3.01, 6.79) * mm, "end": v(3, 6.79) * mm});
            skLineSegment(sketch, "E581", {"start": v(3, 6.79) * mm, "end": v(3, 6.79) * mm});
            skLineSegment(sketch, "E582", {"start": v(3, 6.79) * mm, "end": v(2.99, 6.79) * mm});
            skLineSegment(sketch, "E583", {"start": v(2.99, 6.79) * mm, "end": v(2.98, 6.79) * mm});
            skLineSegment(sketch, "E584", {"start": v(2.98, 6.79) * mm, "end": v(2.98, 6.79) * mm});
            skLineSegment(sketch, "E585", {"start": v(2.98, 6.79) * mm, "end": v(2.97, 6.79) * mm});
            skLineSegment(sketch, "E586", {"start": v(2.97, 6.79) * mm, "end": v(2.97, 6.79) * mm});
            skLineSegment(sketch, "E587", {"start": v(2.97, 6.79) * mm, "end": v(2.96, 6.79) * mm});
            skLineSegment(sketch, "E588", {"start": v(2.96, 6.79) * mm, "end": v(2.96, 6.79) * mm});
            skLineSegment(sketch, "E589", {"start": v(2.96, 6.79) * mm, "end": v(2.95, 6.79) * mm});
            skLineSegment(sketch, "E590", {"start": v(2.95, 6.79) * mm, "end": v(2.95, 6.79) * mm});
            skLineSegment(sketch, "E591", {"start": v(2.95, 6.79) * mm, "end": v(2.94, 6.8) * mm});
            skLineSegment(sketch, "E592", {"start": v(2.94, 6.8) * mm, "end": v(2.94, 6.8) * mm});
            skLineSegment(sketch, "E593", {"start": v(2.94, 6.8) * mm, "end": v(2.93, 6.8) * mm});
            skLineSegment(sketch, "E594", {"start": v(2.93, 6.8) * mm, "end": v(2.93, 6.8) * mm});
            skLineSegment(sketch, "E595", {"start": v(2.93, 6.8) * mm, "end": v(2.92, 6.8) * mm});
            skLineSegment(sketch, "E596", {"start": v(2.92, 6.8) * mm, "end": v(2.92, 6.8) * mm});
            skLineSegment(sketch, "E597", {"start": v(2.92, 6.8) * mm, "end": v(2.91, 6.8) * mm});
            skLineSegment(sketch, "E598", {"start": v(-0.45, 10.34) * mm, "end": v(0.3, 10.35) * mm});
            skLineSegment(sketch, "E599", {"start": v(0, 0) * mm, "end": v(-0.4, 10.34) * mm});
            skLineSegment(sketch, "E600", {"start": v(0, 0) * mm, "end": v(0.28, 10.35) * mm});
            skLineSegment(sketch, "E601", {"start": v(0, 6.3) * mm, "end": v(2.91, 6.8) * mm});
            skLineSegment(sketch, "E602", {"start": v(0, 6.3) * mm, "end": v(2.95, 6.23) * mm});
            skCircle(sketch, "E603", {"center": v(0, 6.3) * mm, "radius": 1.35 * mm});
            skSolve(sketch);
        }
        {
            var Q0;
            {var subQ6=sQuery(id+"F0.wireOp",EDGE,"E423");Q0=makeQuery(id+"F0.imprint","IMPRINT",FACE,{"disambiguationData":[TD([[makeQuery(id+"F0.imprint","IMPRINT",EDGE,{"derivedFrom":subQ6}),1.0]])]});}
            var Q1;
            {var subQ0=sQuery(id+"F0.wireOp",EDGE,"E602");var subQ3=sQuery(id+"F0.wireOp",EDGE,"E3");var subQ4=makeQuery(id+"F0.imprint","INTERSECT",VERTEX,{"derivedFrom":[subQ3,subQ0]});Q1=makeQuery(id+"F0.imprint","IMPRINT",FACE,{"disambiguationData":[TD([[makeQuery(id+"F0.imprint","IMPRINT",EDGE,{"disambiguationData":[TD([[subQ4,1.0]])],"derivedFrom":subQ3}),-1.0]])]});}
            var Q2;
            {var subQ0=sQuery(id+"F0.wireOp",EDGE,"E602");var subQ1=sQuery(id+"F0.wireOp",EDGE,"E600");var subQ2=makeQuery(id+"F0.imprint","INTERSECT",VERTEX,{"derivedFrom":[subQ1,subQ0]});Q2=makeQuery(id+"F0.imprint","IMPRINT",FACE,{"disambiguationData":[TD([[makeQuery(id+"F0.imprint","IMPRINT",EDGE,{"disambiguationData":[TD([[subQ2,-1.0]])],"derivedFrom":subQ1}),1.0]])]});}
            extrude(context, id + "F1", {"entities" : qUnion([Q0, Q1, Q2]), "depth" : 5 * mm});
        }
        {
            var Q0;
            Q0=makeQuery(id+"F1.opExtrude","SWEPT_BODY",BODY,{"disambiguationData":[OSD([sQuery(id+"F0.wireOp",EDGE,"E423"),sQuery(id+"F0.wireOp",EDGE,"E424"),sQuery(id+"F0.wireOp",EDGE,"E425"),sQuery(id+"F0.wireOp",EDGE,"E426"),sQuery(id+"F0.wireOp",EDGE,"E427"),sQuery(id+"F0.wireOp",EDGE,"E428"),sQuery(id+"F0.wireOp",EDGE,"E429"),sQuery(id+"F0.wireOp",EDGE,"E430"),sQuery(id+"F0.wireOp",EDGE,"E430"),sQuery(id+"F0.wireOp",EDGE,"E431"),sQuery(id+"F0.wireOp",EDGE,"E432"),sQuery(id+"F0.wireOp",EDGE,"E433"),sQuery(id+"F0.wireOp",EDGE,"E433"),sQuery(id+"F0.wireOp",EDGE,"E433"),sQuery(id+"F0.wireOp",EDGE,"E434"),sQuery(id+"F0.wireOp",EDGE,"E435"),sQuery(id+"F0.wireOp",EDGE,"E436"),sQuery(id+"F0.wireOp",EDGE,"E436"),sQuery(id+"F0.wireOp",EDGE,"E437"),sQuery(id+"F0.wireOp",EDGE,"E438"),sQuery(id+"F0.wireOp",EDGE,"E439"),sQuery(id+"F0.wireOp",EDGE,"E440"),sQuery(id+"F0.wireOp",EDGE,"E441"),sQuery(id+"F0.wireOp",EDGE,"E442"),sQuery(id+"F0.wireOp",EDGE,"E443"),sQuery(id+"F0.wireOp",EDGE,"E444"),sQuery(id+"F0.wireOp",EDGE,"E444"),sQuery(id+"F0.wireOp",EDGE,"E445"),sQuery(id+"F0.wireOp",EDGE,"E446"),sQuery(id+"F0.wireOp",EDGE,"E447"),sQuery(id+"F0.wireOp",EDGE,"E448"),sQuery(id+"F0.wireOp",EDGE,"E449"),sQuery(id+"F0.wireOp",EDGE,"E450"),sQuery(id+"F0.wireOp",EDGE,"E451"),sQuery(id+"F0.wireOp",EDGE,"E451"),sQuery(id+"F0.wireOp",EDGE,"E451"),sQuery(id+"F0.wireOp",EDGE,"E452"),sQuery(id+"F0.wireOp",EDGE,"E453"),sQuery(id+"F0.wireOp",EDGE,"E454"),sQuery(id+"F0.wireOp",EDGE,"E455"),sQuery(id+"F0.wireOp",EDGE,"E456"),sQuery(id+"F0.wireOp",EDGE,"E457"),sQuery(id+"F0.wireOp",EDGE,"E458"),sQuery(id+"F0.wireOp",EDGE,"E459"),sQuery(id+"F0.wireOp",EDGE,"E460"),sQuery(id+"F0.wireOp",EDGE,"E461"),sQuery(id+"F0.wireOp",EDGE,"E461"),sQuery(id+"F0.wireOp",EDGE,"E462"),sQuery(id+"F0.wireOp",EDGE,"E463"),sQuery(id+"F0.wireOp",EDGE,"E464"),sQuery(id+"F0.wireOp",EDGE,"E465"),sQuery(id+"F0.wireOp",EDGE,"E466"),sQuery(id+"F0.wireOp",EDGE,"E467"),sQuery(id+"F0.wireOp",EDGE,"E467"),sQuery(id+"F0.wireOp",EDGE,"E468"),sQuery(id+"F0.wireOp",EDGE,"E469"),sQuery(id+"F0.wireOp",EDGE,"E470"),sQuery(id+"F0.wireOp",EDGE,"E470"),sQuery(id+"F0.wireOp",EDGE,"E470"),sQuery(id+"F0.wireOp",EDGE,"E471"),sQuery(id+"F0.wireOp",EDGE,"E472"),sQuery(id+"F0.wireOp",EDGE,"E473"),sQuery(id+"F0.wireOp",EDGE,"E473"),sQuery(id+"F0.wireOp",EDGE,"E474"),sQuery(id+"F0.wireOp",EDGE,"E475"),sQuery(id+"F0.wireOp",EDGE,"E476"),sQuery(id+"F0.wireOp",EDGE,"E477"),sQuery(id+"F0.wireOp",EDGE,"E478"),sQuery(id+"F0.wireOp",EDGE,"E479"),sQuery(id+"F0.wireOp",EDGE,"E480"),sQuery(id+"F0.wireOp",EDGE,"E481"),sQuery(id+"F0.wireOp",EDGE,"E482"),sQuery(id+"F0.wireOp",EDGE,"E483"),sQuery(id+"F0.wireOp",EDGE,"E484"),sQuery(id+"F0.wireOp",EDGE,"E485"),sQuery(id+"F0.wireOp",EDGE,"E486"),sQuery(id+"F0.wireOp",EDGE,"E487"),sQuery(id+"F0.wireOp",EDGE,"E488"),sQuery(id+"F0.wireOp",EDGE,"E489"),sQuery(id+"F0.wireOp",EDGE,"E489"),sQuery(id+"F0.wireOp",EDGE,"E489"),sQuery(id+"F0.wireOp",EDGE,"E490"),sQuery(id+"F0.wireOp",EDGE,"E491"),sQuery(id+"F0.wireOp",EDGE,"E492"),sQuery(id+"F0.wireOp",EDGE,"E493"),sQuery(id+"F0.wireOp",EDGE,"E494"),sQuery(id+"F0.wireOp",EDGE,"E495"),sQuery(id+"F0.wireOp",EDGE,"E496"),sQuery(id+"F0.wireOp",EDGE,"E497"),sQuery(id+"F0.wireOp",EDGE,"E498"),sQuery(id+"F0.wireOp",EDGE,"E499"),sQuery(id+"F0.wireOp",EDGE,"E500"),sQuery(id+"F0.wireOp",EDGE,"E501"),sQuery(id+"F0.wireOp",EDGE,"E502"),sQuery(id+"F0.wireOp",EDGE,"E502"),sQuery(id+"F0.wireOp",EDGE,"E503"),sQuery(id+"F0.wireOp",EDGE,"E504"),sQuery(id+"F0.wireOp",EDGE,"E505"),sQuery(id+"F0.wireOp",EDGE,"E506"),sQuery(id+"F0.wireOp",EDGE,"E507"),sQuery(id+"F0.wireOp",EDGE,"E508"),sQuery(id+"F0.wireOp",EDGE,"E509"),sQuery(id+"F0.wireOp",EDGE,"E510"),sQuery(id+"F0.wireOp",EDGE,"E511"),sQuery(id+"F0.wireOp",EDGE,"E512"),sQuery(id+"F0.wireOp",EDGE,"E513"),sQuery(id+"F0.wireOp",EDGE,"E514"),sQuery(id+"F0.wireOp",EDGE,"E515"),sQuery(id+"F0.wireOp",EDGE,"E516"),sQuery(id+"F0.wireOp",EDGE,"E517"),sQuery(id+"F0.wireOp",EDGE,"E518"),sQuery(id+"F0.wireOp",EDGE,"E519"),sQuery(id+"F0.wireOp",EDGE,"E520"),sQuery(id+"F0.wireOp",EDGE,"E521"),sQuery(id+"F0.wireOp",EDGE,"E522"),sQuery(id+"F0.wireOp",EDGE,"E523"),sQuery(id+"F0.wireOp",EDGE,"E524"),sQuery(id+"F0.wireOp",EDGE,"E524"),sQuery(id+"F0.wireOp",EDGE,"E525"),sQuery(id+"F0.wireOp",EDGE,"E526"),sQuery(id+"F0.wireOp",EDGE,"E527"),sQuery(id+"F0.wireOp",EDGE,"E528"),sQuery(id+"F0.wireOp",EDGE,"E529"),sQuery(id+"F0.wireOp",EDGE,"E530"),sQuery(id+"F0.wireOp",EDGE,"E531"),sQuery(id+"F0.wireOp",EDGE,"E532"),sQuery(id+"F0.wireOp",EDGE,"E533"),sQuery(id+"F0.wireOp",EDGE,"E534"),sQuery(id+"F0.wireOp",EDGE,"E535"),sQuery(id+"F0.wireOp",EDGE,"E536"),sQuery(id+"F0.wireOp",EDGE,"E537"),sQuery(id+"F0.wireOp",EDGE,"E538"),sQuery(id+"F0.wireOp",EDGE,"E539"),sQuery(id+"F0.wireOp",EDGE,"E540"),sQuery(id+"F0.wireOp",EDGE,"E541"),sQuery(id+"F0.wireOp",EDGE,"E542"),sQuery(id+"F0.wireOp",EDGE,"E543"),sQuery(id+"F0.wireOp",EDGE,"E544"),sQuery(id+"F0.wireOp",EDGE,"E544"),sQuery(id+"F0.wireOp",EDGE,"E544"),sQuery(id+"F0.wireOp",EDGE,"E544"),sQuery(id+"F0.wireOp",EDGE,"E545"),sQuery(id+"F0.wireOp",EDGE,"E546"),sQuery(id+"F0.wireOp",EDGE,"E547"),sQuery(id+"F0.wireOp",EDGE,"E548"),sQuery(id+"F0.wireOp",EDGE,"E549"),sQuery(id+"F0.wireOp",EDGE,"E550"),sQuery(id+"F0.wireOp",EDGE,"E551"),sQuery(id+"F0.wireOp",EDGE,"E552"),sQuery(id+"F0.wireOp",EDGE,"E553"),sQuery(id+"F0.wireOp",EDGE,"E554"),sQuery(id+"F0.wireOp",EDGE,"E555"),sQuery(id+"F0.wireOp",EDGE,"E556"),sQuery(id+"F0.wireOp",EDGE,"E557"),sQuery(id+"F0.wireOp",EDGE,"E557"),sQuery(id+"F0.wireOp",EDGE,"E558"),sQuery(id+"F0.wireOp",EDGE,"E559"),sQuery(id+"F0.wireOp",EDGE,"E560"),sQuery(id+"F0.wireOp",EDGE,"E561"),sQuery(id+"F0.wireOp",EDGE,"E562"),sQuery(id+"F0.wireOp",EDGE,"E562"),sQuery(id+"F0.wireOp",EDGE,"E562"),sQuery(id+"F0.wireOp",EDGE,"E563"),sQuery(id+"F0.wireOp",EDGE,"E564"),sQuery(id+"F0.wireOp",EDGE,"E565"),sQuery(id+"F0.wireOp",EDGE,"E566"),sQuery(id+"F0.wireOp",EDGE,"E567"),sQuery(id+"F0.wireOp",EDGE,"E568"),sQuery(id+"F0.wireOp",EDGE,"E569"),sQuery(id+"F0.wireOp",EDGE,"E570"),sQuery(id+"F0.wireOp",EDGE,"E571"),sQuery(id+"F0.wireOp",EDGE,"E572"),sQuery(id+"F0.wireOp",EDGE,"E573"),sQuery(id+"F0.wireOp",EDGE,"E574"),sQuery(id+"F0.wireOp",EDGE,"E575"),sQuery(id+"F0.wireOp",EDGE,"E576"),sQuery(id+"F0.wireOp",EDGE,"E577"),sQuery(id+"F0.wireOp",EDGE,"E578"),sQuery(id+"F0.wireOp",EDGE,"E579"),sQuery(id+"F0.wireOp",EDGE,"E580"),sQuery(id+"F0.wireOp",EDGE,"E581"),sQuery(id+"F0.wireOp",EDGE,"E581"),sQuery(id+"F0.wireOp",EDGE,"E581"),sQuery(id+"F0.wireOp",EDGE,"E581"),sQuery(id+"F0.wireOp",EDGE,"E582"),sQuery(id+"F0.wireOp",EDGE,"E583"),sQuery(id+"F0.wireOp",EDGE,"E584"),sQuery(id+"F0.wireOp",EDGE,"E585"),sQuery(id+"F0.wireOp",EDGE,"E586"),sQuery(id+"F0.wireOp",EDGE,"E587"),sQuery(id+"F0.wireOp",EDGE,"E588"),sQuery(id+"F0.wireOp",EDGE,"E589"),sQuery(id+"F0.wireOp",EDGE,"E590"),sQuery(id+"F0.wireOp",EDGE,"E590"),sQuery(id+"F0.wireOp",EDGE,"E591"),sQuery(id+"F0.wireOp",EDGE,"E592"),sQuery(id+"F0.wireOp",EDGE,"E593"),sQuery(id+"F0.wireOp",EDGE,"E594"),sQuery(id+"F0.wireOp",EDGE,"E595"),sQuery(id+"F0.wireOp",EDGE,"E596"),sQuery(id+"F0.wireOp",EDGE,"E597"),sQuery(id+"F0.wireOp",EDGE,"E601"),sQuery(id+"F0.wireOp",EDGE,"E602")])]});
            var Q1;
            Q1=makeQuery(id+"F1.opExtrude","SWEPT_EDGE",EDGE,{"disambiguationData":[OSD([sQuery(id+"F0.wireOp",EDGE,"E601"),sQuery(id+"F0.wireOp",EDGE,"E602")])]});
            circularPattern(context, id + "F2", {"operationType" : NewBodyOperationType.ADD, "entities" : qUnion([Q0]), "axis" : qUnion([Q1]), "angle" : 11.25 * degree, "instanceCount" : round(32)});
        }
    });
